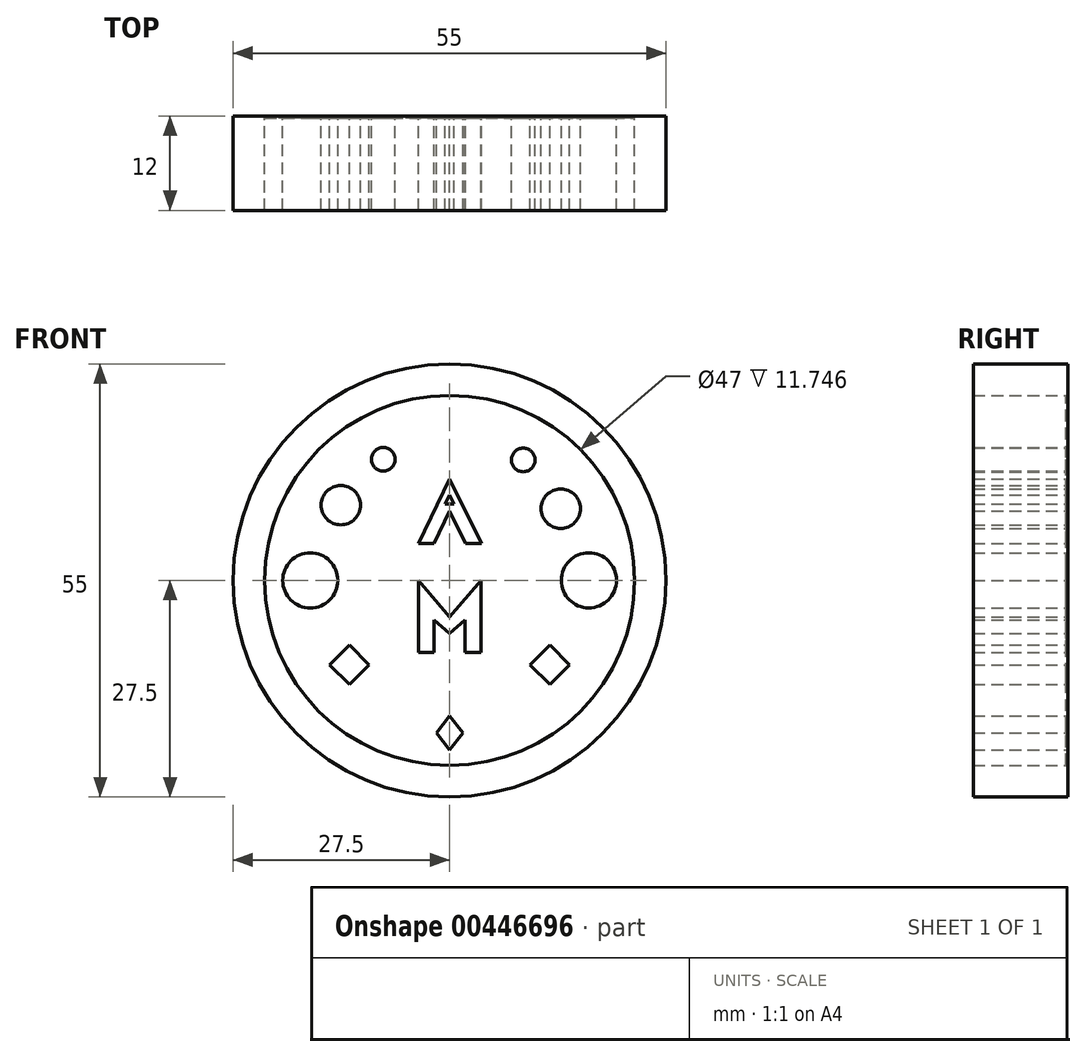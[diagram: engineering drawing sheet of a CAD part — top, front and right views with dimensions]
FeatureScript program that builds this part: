
annotation { "Feature Type Name" : "Feature", "Feature Type Description" : "" }
export const myFeature = defineFeature(function(context is Context, id is Id, definition is map)
    precondition{}
    {
        {
            var Q0;
            Q0=qCreatedBy(makeId("Front.planeOp"),FACE);
            var sketch = newSketch(context, id + "F0", { "sketchPlane" : qUnion([Q0])});
            skCircle(sketch, "E0", {"center": v(0, 0) * mm, "radius": 27.5 * mm});
            skCircle(sketch, "E1", {"center": v(0, 0) * mm, "radius": 23.5 * mm});
            skSolve(sketch);
        }
        {
            var Q0;
            Q0=makeQuery(id+"F0.imprint","IMPRINT",FACE,{"disambiguationData":[TD([[makeQuery(id+"F0.imprint","IMPRINT",EDGE,{"derivedFrom":sQuery(id+"F0.wireOp",EDGE,"E0")}),1.0]])]});
            extrude(context, id + "F1", {"entities" : qUnion([Q0]), "depth" : 12 * mm});
        }
        {
            var Q0;
            Q0=qCreatedBy(makeId("Front.planeOp"),FACE);
            var sketch = newSketch(context, id + "F2", { "sketchPlane" : qUnion([Q0])});
            skCircle(sketch, "E2", {"center": v(0, 0) * mm, "radius": 27.47 * mm});
            skSolve(sketch);
        }
        {
            var Q0;
            Q0 = qSketchRegion(id + "F2", true);
            extrude(context, id + "F3", {"entities" : qUnion([Q0]), "operationType" : NewBodyOperationType.ADD, "depth" : 0.25 * mm});
        }
        {
            var Q0;
            Q0=qCreatedBy(makeId("Front.planeOp"),FACE);
            var sketch = newSketch(context, id + "F4", { "sketchPlane" : qUnion([Q0])});
            skCircle(sketch, "E3", {"center": v(17.69, 0.01) * mm, "radius": 3.5 * mm});
            skCircle(sketch, "E4", {"center": v(-17.7, 0) * mm, "radius": 3.5 * mm});
            skCircle(sketch, "E5", {"center": v(-13.82, 9.57) * mm, "radius": 2.5 * mm});
            skCircle(sketch, "E6", {"center": v(-8.43, 15.39) * mm, "radius": 1.5 * mm});
            skCircle(sketch, "E7", {"center": v(9.35, 15.3) * mm, "radius": 1.5 * mm});
            skCircle(sketch, "E8", {"center": v(14.12, 9.12) * mm, "radius": 2.5 * mm});
            skSolve(sketch);
        }
        {
            var Q0;
            Q0 = qSketchRegion(id + "F4", true);
            extrude(context, id + "F5", {"entities" : qUnion([Q0]), "operationType" : NewBodyOperationType.ADD, "depth" : 12 * mm});
        }
        {
            var Q0;
            Q0=qCreatedBy(makeId("Front.planeOp"),FACE);
            var sketch = newSketch(context, id + "F6", { "sketchPlane" : qUnion([Q0])});
            skLineSegment(sketch, "E9", {"start": v(0, 12.91) * mm, "end": v(-3.98, 4.72) * mm});
            skLineSegment(sketch, "E10", {"start": v(-3.98, 4.72) * mm, "end": v(0, 12.91) * mm});
            skLineSegment(sketch, "E11", {"start": v(4.06, 4.72) * mm, "end": v(0, 12.91) * mm});
            skLineSegment(sketch, "E12", {"start": v(-3.98, 4.72) * mm, "end": v(-1.99, 4.72) * mm});
            skPoint(sketch, "E12.endSnap0", {"position": v(-1.99, 8.82) * mm});
            skLineSegment(sketch, "E13", {"start": v(4.06, 4.72) * mm, "end": v(2.03, 4.72) * mm});
            skPoint(sketch, "E13.endSnap0", {"position": v(2.03, 8.82) * mm});
            skLineSegment(sketch, "E14", {"start": v(2.03, 4.72) * mm, "end": v(0, 8.82) * mm});
            skLineSegment(sketch, "E15", {"start": v(0, 8.82) * mm, "end": v(-1.99, 4.72) * mm});
            skLineSegment(sketch, "E16", {"start": v(0, 10.88) * mm, "end": v(-0.55, 9.74) * mm});
            skLineSegment(sketch, "E17", {"start": v(-0.55, 9.74) * mm, "end": v(0.55, 9.74) * mm});
            skLineSegment(sketch, "E18", {"start": v(0.55, 9.74) * mm, "end": v(0, 10.88) * mm});
            skLineSegment(sketch, "E19", {"start": v(-3.98, 0) * mm, "end": v(-3.98, -9.14) * mm});
            skLineSegment(sketch, "E20", {"start": v(-3.98, 0) * mm, "end": v(0, -4.62) * mm});
            skLineSegment(sketch, "E21", {"start": v(0, -4.62) * mm, "end": v(3.98, 0) * mm});
            skLineSegment(sketch, "E22", {"start": v(3.98, 0) * mm, "end": v(3.98, -9.14) * mm});
            skLineSegment(sketch, "E23", {"start": v(-3.98, -9.14) * mm, "end": v(-1.99, -9.14) * mm});
            skPoint(sketch, "E23.endSnap0", {"position": v(-1.99, -2.3) * mm});
            skLineSegment(sketch, "E24", {"start": v(3.98, -9.14) * mm, "end": v(1.99, -9.14) * mm});
            skPoint(sketch, "E24.endSnap0", {"position": v(1.99, -2.3) * mm});
            skLineSegment(sketch, "E25", {"start": v(1.99, -9.14) * mm, "end": v(1.99, -5.04) * mm});
            skLineSegment(sketch, "E26", {"start": v(1.99, -5.04) * mm, "end": v(0, -6.75) * mm});
            skLineSegment(sketch, "E27", {"start": v(-1.99, -9.14) * mm, "end": v(-1.99, -5.04) * mm});
            skLineSegment(sketch, "E28", {"start": v(-1.99, -5.04) * mm, "end": v(0, -6.75) * mm});
            skSolve(sketch);
        }
        {
            var Q0;
            Q0 = qSketchRegion(id + "F6", true);
            extrude(context, id + "F7", {"entities" : qUnion([Q0]), "operationType" : NewBodyOperationType.ADD, "depth" : 12 * mm});
        }
        {
            var Q0;
            Q0=qCreatedBy(makeId("Front.planeOp"),FACE);
            var sketch = newSketch(context, id + "F8", { "sketchPlane" : qUnion([Q0])});
            skLineSegment(sketch, "E29", {"start": v(-12.73, -8.2) * mm, "end": v(-15.24, -10.71) * mm});
            skLineSegment(sketch, "E30", {"start": v(-15.24, -10.71) * mm, "end": v(-12.73, -13.23) * mm});
            skLineSegment(sketch, "E31", {"start": v(-12.73, -13.23) * mm, "end": v(-10.21, -10.71) * mm});
            skLineSegment(sketch, "E32", {"start": v(-10.21, -10.71) * mm, "end": v(-12.73, -8.2) * mm});
            skLineSegment(sketch, "E33", {"start": v(10.21, -10.71) * mm, "end": v(12.73, -8.2) * mm});
            skLineSegment(sketch, "E34", {"start": v(12.73, -8.2) * mm, "end": v(15.24, -10.71) * mm});
            skLineSegment(sketch, "E35", {"start": v(15.24, -10.71) * mm, "end": v(12.73, -13.23) * mm});
            skLineSegment(sketch, "E36", {"start": v(12.73, -13.23) * mm, "end": v(10.21, -10.71) * mm});
            skLineSegment(sketch, "E37", {"start": v(0, -17.22) * mm, "end": v(-1.64, -19.36) * mm});
            skLineSegment(sketch, "E38", {"start": v(-1.64, -19.36) * mm, "end": v(0, -21.5) * mm});
            skLineSegment(sketch, "E39", {"start": v(0, -21.5) * mm, "end": v(1.73, -19.36) * mm});
            skLineSegment(sketch, "E40", {"start": v(1.73, -19.36) * mm, "end": v(0, -17.22) * mm});
            skSolve(sketch);
        }
        {
            var Q0;
            Q0 = qSketchRegion(id + "F8", true);
            extrude(context, id + "F9", {"entities" : qUnion([Q0]), "operationType" : NewBodyOperationType.ADD, "depth" : 12 * mm});
        }
    });
